# Revit family: Geräteeinsätze GES_Geräteeinsatz_GES4_mit_Rastschieber
name_source: partatom
category: Generic Models
revit_build: Autodesk Revit 2015 (Build: 20140606_1530(x64)
units: mm (PartAtom-declared; Revit-internal decimal feet)

## types (3) — shared parameters
Height = 61 mm  [stored 0.200131 ft]
Inner cut = 16 mm  [stored 0.0524934 ft]
Inner cut2 = 17 mm
Manufacturer = OBO Bettermann
Snur width = 90 mm  [stored 0.295276 ft]
URL = http://www.obo-bettermann.com
Width = 222 mm  [stored 0.728346 ft]
Width 2 = 200 mm  [stored 0.656168 ft]

## per-type parameters (varying)
| type | Article Type | GTIN | Manufacturer Art. No. | Material |
| GES4-2U10T 9011 | GES42U10T 9011 | 4012195890676 | 7405146 | Plastic RAL 9011 |
| GES4-2U10T 7011 | GES4-2U10T 7011 | 4012195890645 | 7405145 | Plastic RAL 7011 |
| GES4-2U10T 1019 | GES4-2U10T 1019 | 4012195890683 | 7405147 | Plastic RAL 1019 |

note: [stored X ft] marks values corroborated as IEEE doubles in the binary element streams (Revit-internal decimal feet)

## geometry (parser evidence)
native form markers: Sweep x2
no freeform markers — native parametric forms only
